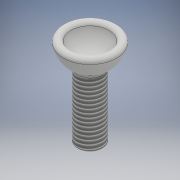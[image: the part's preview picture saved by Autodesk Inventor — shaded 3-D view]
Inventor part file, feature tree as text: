
AUTODESK INVENTOR PART (.ipt)
format: ipt  version: 2018 (Build 220112000, 112)  size: 173,056 bytes
history: native  units: mm
features: fillet x2, sketch x2, revolve x1, extrude x1, thread x1
ambient origin geometry x8: Origin, YZ Plane, XZ Plane, XY Plane, X Axis, Y Axis, Z Axis, Center Point
bodies: Solid1 (feature_tree)
feature tree (7):
  revolve  "Revolution1"  [1 undecoded]
  extrude  "Extrusion1"  Depth=3.5mm
  fillet  "Fillet1"  Radius=0.5mm
  fillet  "Fillet2"  [1 undecoded]
  thread  "Thread2"  [1 undecoded]
  sketch  "Sketch1"  dims[d0=11.75mm d1=1.625mm]
  sketch  "Sketch2"  dims[d2=2.5mm d3=3.5mm d4=0.5mm d5=90.0deg d6=2.0mm d7=1.5mm d8=0.0mm d9=0.2mm d10=0.5mm d13=8.161mm d14=0.0mm]
note: 3 required parameter values undecoded (feature->parameter linkage not recoverable at this tier; creation-order binding heuristic only, values carry confidence <= 0.55)